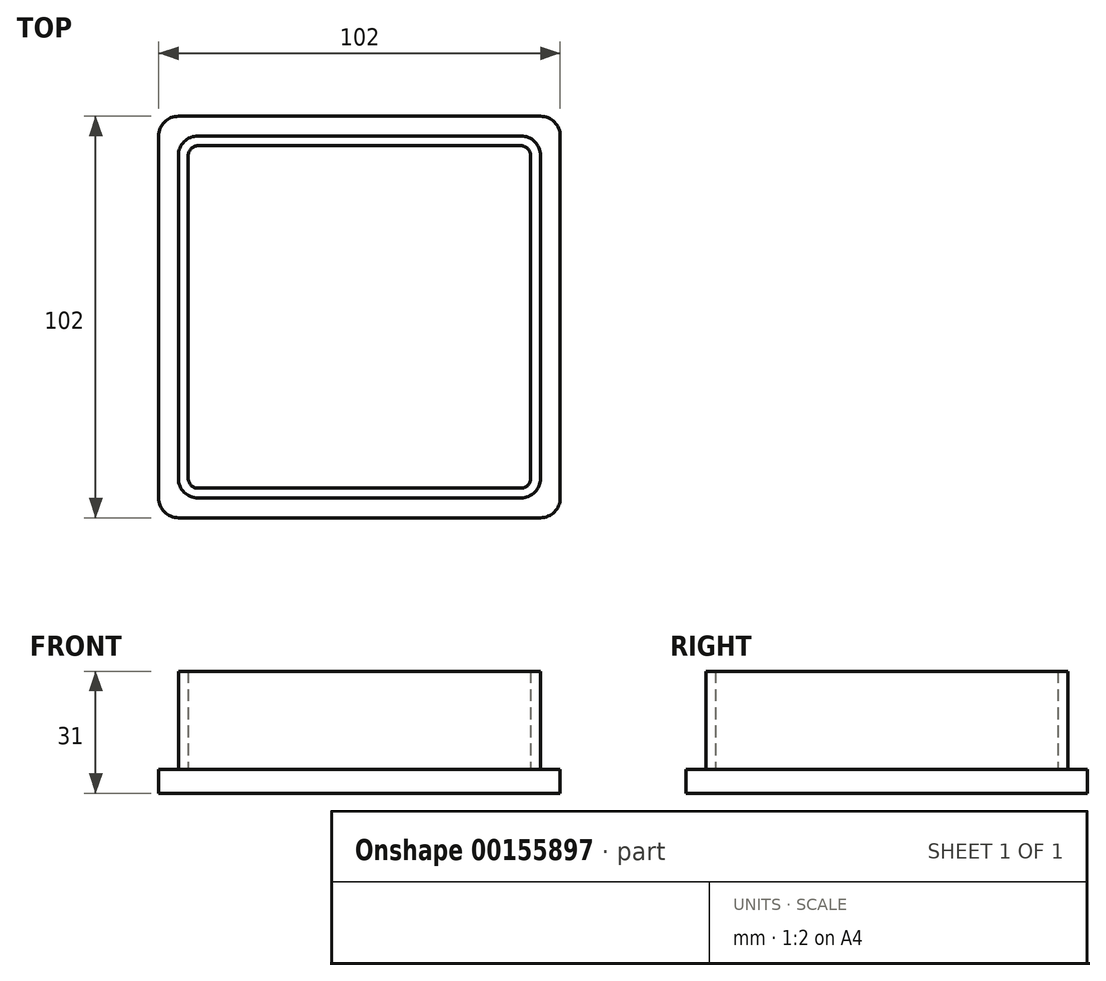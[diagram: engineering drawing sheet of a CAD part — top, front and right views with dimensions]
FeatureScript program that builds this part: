
annotation { "Feature Type Name" : "Feature", "Feature Type Description" : "" }
export const myFeature = defineFeature(function(context is Context, id is Id, definition is map)
    precondition{}
    {
        {
            var Q0;
            Q0=qCreatedBy(makeId("Top.planeOp"),FACE);
            var sketch = newSketch(context, id + "F0", { "sketchPlane" : qUnion([Q0])});
            skLineSegment(sketch, "E0.bottom", {"start": v(51, -51) * mm, "end": v(-51, -51) * mm});
            skLineSegment(sketch, "E0.top", {"start": v(51, 51) * mm, "end": v(-51, 51) * mm});
            skLineSegment(sketch, "E0.left", {"start": v(51, -51) * mm, "end": v(51, 51) * mm});
            skLineSegment(sketch, "E0.right", {"start": v(-51, -51) * mm, "end": v(-51, 51) * mm});
            skPoint(sketch, "E0.middle", {"position": v(0, 0) * mm});
            skSolve(sketch);
        }
        {
            var Q0;
            Q0=makeQuery(id+"F0.imprint","IMPRINT",FACE,{"disambiguationData":[TD([[makeQuery(id+"F0.imprint","IMPRINT",EDGE,{"derivedFrom":sQuery(id+"F0.wireOp",EDGE,"E0.bottom")}),-1.0]])]});
            extrude(context, id + "F1", {"entities" : qUnion([Q0]), "depth" : 3 * mm});
        }
        {
            var Q0;
            Q0=makeQuery(id+"F1.opExtrude","SWEPT_EDGE",EDGE,{"disambiguationData":[OSD([sQuery(id+"F0.wireOp",EDGE,"E0.bottom"),sQuery(id+"F0.wireOp",EDGE,"E0.right")])]});
            var Q1;
            Q1=makeQuery(id+"F1.opExtrude","SWEPT_EDGE",EDGE,{"disambiguationData":[OSD([sQuery(id+"F0.wireOp",EDGE,"E0.bottom"),sQuery(id+"F0.wireOp",EDGE,"E0.left")])]});
            var Q2;
            Q2=makeQuery(id+"F1.opExtrude","SWEPT_EDGE",EDGE,{"disambiguationData":[OSD([sQuery(id+"F0.wireOp",EDGE,"E0.top"),sQuery(id+"F0.wireOp",EDGE,"E0.left")])]});
            fillet(context, id + "F2", {"entities" : qUnion([Q0, Q1, Q2]), "radius" : 5 * mm, "tangentPropagation" : true, "allowEdgeOverflow" : false});
        }
        {
            var Q0;
            Q0=makeQuery(id+"FnozJgRAO8CeqoZ_1.opExtrude","SWEPT_EDGE",EDGE,{"disambiguationData":[OSD([sQuery(id+"F3bBfRw1wlHWd7v_1.wireOp",EDGE,"W9GcecPn-69S4-2BQ7-XzoK-HypjezHoQNqc.top"),sQuery(id+"F3bBfRw1wlHWd7v_1.wireOp",EDGE,"W9GcecPn-69S4-2BQ7-XzoK-HypjezHoQNqc.right")])]});
            var Q1;
            Q1=makeQuery(id+"FnozJgRAO8CeqoZ_1.opExtrude","SWEPT_EDGE",EDGE,{"disambiguationData":[OSD([sQuery(id+"F3bBfRw1wlHWd7v_1.wireOp",EDGE,"W9GcecPn-69S4-2BQ7-XzoK-HypjezHoQNqc.bottom"),sQuery(id+"F3bBfRw1wlHWd7v_1.wireOp",EDGE,"W9GcecPn-69S4-2BQ7-XzoK-HypjezHoQNqc.right")])]});
            var Q2;
            Q2=makeQuery(id+"FnozJgRAO8CeqoZ_1.opExtrude","SWEPT_EDGE",EDGE,{"disambiguationData":[OSD([sQuery(id+"F3bBfRw1wlHWd7v_1.wireOp",EDGE,"W9GcecPn-69S4-2BQ7-XzoK-HypjezHoQNqc.bottom"),sQuery(id+"F3bBfRw1wlHWd7v_1.wireOp",EDGE,"W9GcecPn-69S4-2BQ7-XzoK-HypjezHoQNqc.left")])]});
            var Q3;
            Q3=makeQuery(id+"FnozJgRAO8CeqoZ_1.opExtrude","SWEPT_EDGE",EDGE,{"disambiguationData":[OSD([sQuery(id+"F3bBfRw1wlHWd7v_1.wireOp",EDGE,"W9GcecPn-69S4-2BQ7-XzoK-HypjezHoQNqc.top"),sQuery(id+"F3bBfRw1wlHWd7v_1.wireOp",EDGE,"W9GcecPn-69S4-2BQ7-XzoK-HypjezHoQNqc.left")])]});
            var Q4;
            Q4=makeQuery(id+"F1.opExtrude","SWEPT_EDGE",EDGE,{"disambiguationData":[OSD([sQuery(id+"F0.wireOp",EDGE,"E0.top"),sQuery(id+"F0.wireOp",EDGE,"E0.right")])]});
            fillet(context, id + "F3", {"entities" : qUnion([Q0, Q1, Q2, Q3, Q4]), "radius" : 5 * mm, "tangentPropagation" : true, "allowEdgeOverflow" : false});
        }
        {
            var Q0;
            Q0=makeQuery(id+"F1.opExtrude","CAP_FACE",FACE,{"disambiguationData":[OSD([sQuery(id+"F0.wireOp",EDGE,"E0.bottom"),sQuery(id+"F0.wireOp",EDGE,"E0.top"),sQuery(id+"F0.wireOp",EDGE,"E0.left"),sQuery(id+"F0.wireOp",EDGE,"E0.right")])],"isStart":false});
            var sketch = newSketch(context, id + "F4", { "sketchPlane" : qUnion([Q0])});
            skLineSegment(sketch, "E1.bottom", {"start": v(46, 46) * mm, "end": v(-46, 46) * mm});
            skLineSegment(sketch, "E1.top", {"start": v(46, -46) * mm, "end": v(-46, -46) * mm});
            skLineSegment(sketch, "E1.left", {"start": v(46, 46) * mm, "end": v(46, -46) * mm});
            skLineSegment(sketch, "E1.right", {"start": v(-46, 46) * mm, "end": v(-46, -46) * mm});
            skPoint(sketch, "E1.middle", {"position": v(0, 0) * mm});
            skSolve(sketch);
        }
        {
            var Q0;
            Q0 = qSketchRegion(id + "F4", true);
            extrude(context, id + "F5", {"entities" : qUnion([Q0]), "operationType" : NewBodyOperationType.ADD, "depth" : 28 * mm});
        }
        {
            var Q0;
            Q0=makeQuery(id+"F5.opExtrude","SWEPT_EDGE",EDGE,{"disambiguationData":[OSD([sQuery(id+"F4.wireOp",EDGE,"E1.top"),sQuery(id+"F4.wireOp",EDGE,"E1.right")])]});
            fillet(context, id + "F6", {"entities" : qUnion([Q0]), "radius" : 5 * mm, "tangentPropagation" : true, "allowEdgeOverflow" : false});
        }
        {
            var Q0;
            Q0=makeQuery(id+"F5.opExtrude","SWEPT_EDGE",EDGE,{"disambiguationData":[OSD([sQuery(id+"F4.wireOp",EDGE,"E1.top"),sQuery(id+"F4.wireOp",EDGE,"E1.left")])]});
            var Q1;
            Q1=makeQuery(id+"F5.opExtrude","SWEPT_EDGE",EDGE,{"disambiguationData":[OSD([sQuery(id+"F4.wireOp",EDGE,"E1.bottom"),sQuery(id+"F4.wireOp",EDGE,"E1.left")])]});
            var Q2;
            Q2=makeQuery(id+"F5.opExtrude","SWEPT_EDGE",EDGE,{"disambiguationData":[OSD([sQuery(id+"F4.wireOp",EDGE,"E1.bottom"),sQuery(id+"F4.wireOp",EDGE,"E1.right")])]});
            fillet(context, id + "F7", {"entities" : qUnion([Q0, Q1, Q2]), "radius" : 5 * mm, "tangentPropagation" : true, "allowEdgeOverflow" : false});
        }
        {
            var Q0;
            Q0=makeQuery(id+"F5.opExtrude","CAP_FACE",FACE,{"disambiguationData":[OSD([sQuery(id+"F4.wireOp",EDGE,"E1.bottom"),sQuery(id+"F4.wireOp",EDGE,"E1.top"),sQuery(id+"F4.wireOp",EDGE,"E1.left"),sQuery(id+"F4.wireOp",EDGE,"E1.right")])],"isStart":false});
            shell(context, id + "F8", {"entities" : qUnion([Q0]), "thickness" : 2.5 * mm});
        }
        {
            var Q0;
            Q0=makeQuery(id+"F1.opExtrude","CAP_FACE",FACE,{"disambiguationData":[OSD([sQuery(id+"F0.wireOp",EDGE,"E0.bottom"),sQuery(id+"F0.wireOp",EDGE,"E0.top"),sQuery(id+"F0.wireOp",EDGE,"E0.left"),sQuery(id+"F0.wireOp",EDGE,"E0.right")])],"isStart":false});
            var Q1;
            Q1=makeQuery(id+"F8.opShell","OFFSET_FACE",FACE,{"disambiguationData":[OSD([sQuery(id+"F0.wireOp",EDGE,"E0.bottom"),sQuery(id+"F0.wireOp",EDGE,"E0.top"),sQuery(id+"F0.wireOp",EDGE,"E0.left"),sQuery(id+"F0.wireOp",EDGE,"E0.right")])]});
            extrude(context, id + "F9", {"entities" : qUnion([Q0, Q1]), "operationType" : NewBodyOperationType.ADD, "depth" : 3 * mm});
        }
        {
            var Q0;
            {var subQ0=sQuery(id+"F0.wireOp",EDGE,"E0.right");var subQ1=sQuery(id+"F0.wireOp",EDGE,"E0.left");var subQ2=sQuery(id+"F0.wireOp",EDGE,"E0.top");var subQ3=sQuery(id+"F0.wireOp",EDGE,"E0.bottom");Q0=makeQuery(id+"F9.opExtrude","CAP_FACE",FACE,{"disambiguationData":[OSD([subQ3,subQ2,subQ1,subQ0]),TDD([makeQuery(id+"F8.opShell","OFFSET_FACE",FACE,{"disambiguationData":[OSD([subQ3,subQ2,subQ1,subQ0])]})])],"isStart":false});}
            var Q1;
            {var subQ0=sQuery(id+"F0.wireOp",EDGE,"E0.right");var subQ1=sQuery(id+"F0.wireOp",EDGE,"E0.left");var subQ2=sQuery(id+"F0.wireOp",EDGE,"E0.top");var subQ3=sQuery(id+"F0.wireOp",EDGE,"E0.bottom");Q1=makeQuery(id+"F9.opExtrude","CAP_FACE",FACE,{"disambiguationData":[OSD([subQ3,subQ2,subQ1,subQ0]),TDD([makeQuery(id+"F1.opExtrude","CAP_FACE",FACE,{"disambiguationData":[OSD([subQ3,subQ2,subQ1,subQ0])],"isStart":false})])],"isStart":false});}
            extrude(context, id + "F10", {"entities" : qUnion([Q0]), "operationType" : NewBodyOperationType.ADD, "endBound" : BoundingType.UP_TO_SURFACE, "endBoundEntityFace" : qUnion([Q1]), "depth" : 25 * mm});
        }
    });
